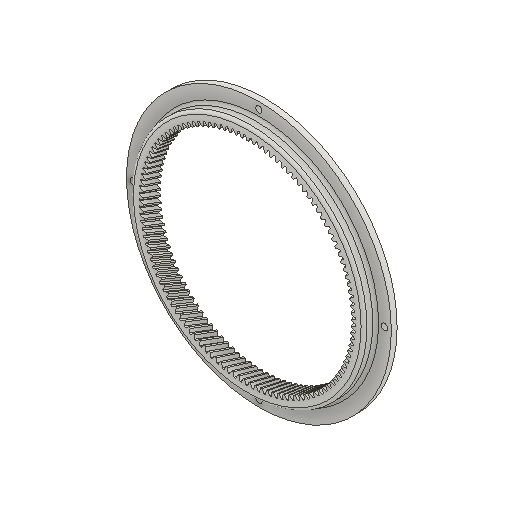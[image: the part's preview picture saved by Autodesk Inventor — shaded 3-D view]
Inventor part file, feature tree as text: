
AUTODESK INVENTOR PART (.ipt)
format: ipt  version: 2025.1 (Build 291241020, 241B)  size: 1,574,400 bytes
history: native  units: mm (DEFAULTED — no unit token found)
features: plane x3, other x3, sketch x3, extrude x2, hole x1, fillet x1
ambient origin geometry x8: Origin, YZ Plane, XZ Plane, XY Plane, X Axis, Y Axis, Z Axis, Center Point
bodies: Solid1 (feature_tree)
feature tree (13):
  extrude  "Extrusion1"  Depth=15.0mm TaperAngle=0.0deg
  plane  "Work Plane2"
  plane  "Work Plane8"
  plane  "Work Plane9"
  other  "Spur Gear"
  extrude  "Extrusion2"  Depth=10.0mm TaperAngle=0.0deg
  hole  "Hole3"  [1 undecoded]
  fillet  "Fillet1"  [1 undecoded]
  sketch  "Sketch1"  dims[d0=200.974857mm d1=15.0mm d2=0.0mm]
  other  "Srf1"
  sketch  "Sketch3"  dims[d3=182.181914mm d4=10.0mm d5=0.0mm]
  sketch  "Sketch6"  dims[d16=63.909111mm d17=0.0mm d34=0.278017mm d39=0.0mm d45=0.0mm d47=63.909111mm d50=0.0mm d51=0.0mm d52=63.909111mm d53=5.0mm d54=0.0mm d69=5.5mm d70=6.0mm d71=4.0mm d72=2.0mm d73=90.0deg d74=8.0mm d75=20.594885mm d76=216.4mm d77=216.4mm d78=108.2mm d79=108.2mm d80=2.5mm d81=228.0mm]
  other  "Pitch Diameter"
note: 2 required parameter values undecoded (feature->parameter linkage not recoverable at this tier; creation-order binding heuristic only, values carry confidence <= 0.55)
